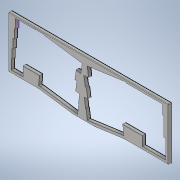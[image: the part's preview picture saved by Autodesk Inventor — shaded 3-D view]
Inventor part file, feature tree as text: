
AUTODESK INVENTOR PART (.ipt)
format: ipt  version: 2022 (Build 260153000, 153)  size: 295,424 bytes
history: mixed  units: in
note: dims shown in document units (in); Inventor stores cm internally (conversion verified against a paired STEP export)
features: fillet x1, sketch x1, imported_body x1
ambient origin geometry x8: Origin, YZ Plane, XZ Plane, XY Plane, X Axis, Y Axis, Z Axis, Center Point
bodies: Solid1 (imported_parasolid), Body3 (imported_parasolid), Solid2 (imported_parasolid)
feature tree (3):
  fillet  "Fillet1"  Radius=0.0394in
  sketch  "Sketch1"
  imported_body  NMx_Import_Brep_tag  [imported B-rep: ~58 faces, bbox_mm=[317.227862, 115.578317, 6.35]]
